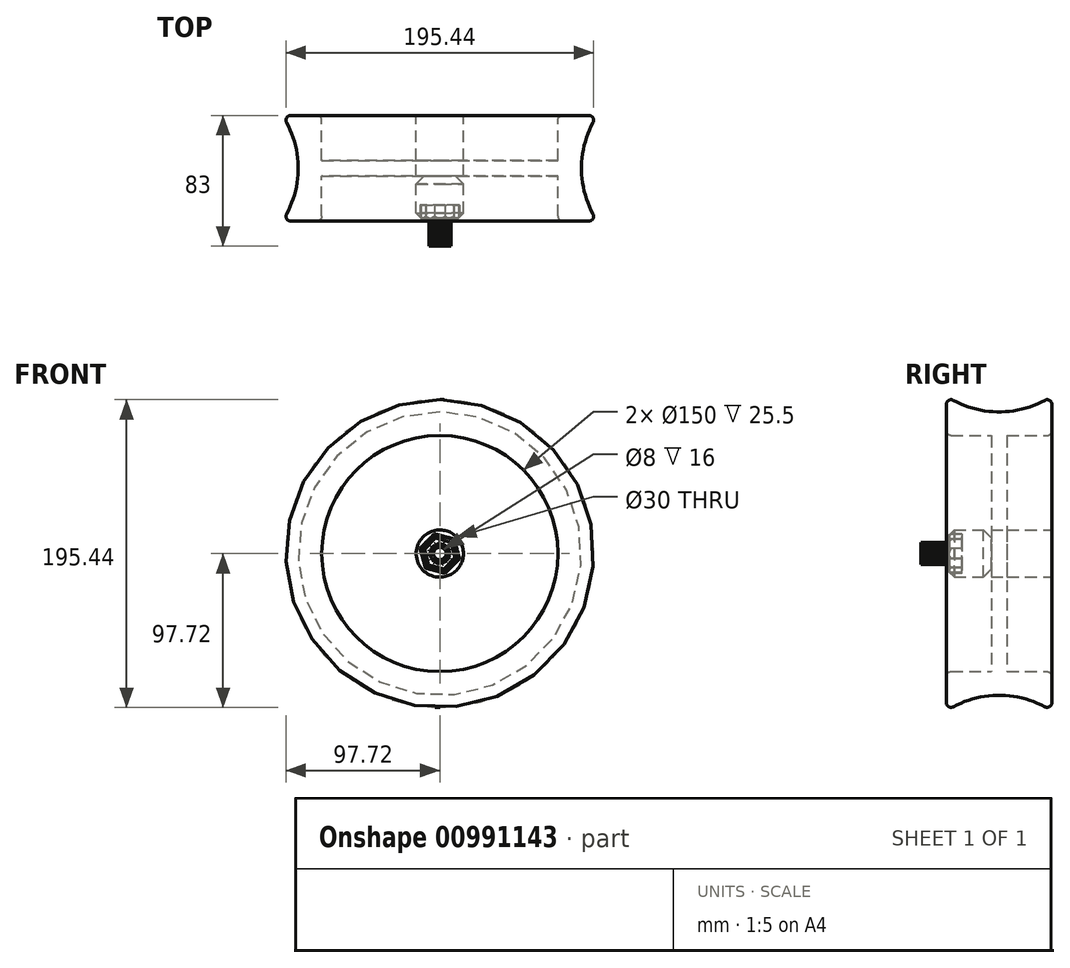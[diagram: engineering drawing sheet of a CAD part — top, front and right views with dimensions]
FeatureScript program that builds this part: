
annotation { "Feature Type Name" : "Feature", "Feature Type Description" : "" }
export const myFeature = defineFeature(function(context is Context, id is Id, definition is map)
    precondition{}
    {
        {
            var Q0;
            Q0=qCreatedBy(makeId("Right.planeOp"),FACE);
            var sketch = newSketch(context, id + "F0", { "sketchPlane" : qUnion([Q0])});
            skPoint(sketch, "E0", {"position": v(0, 90) * mm});
            skLineSegment(sketch, "E1.bottom", {"start": v(33.5, 100) * mm, "end": v(-33.5, 100) * mm});
            skLineSegment(sketch, "E1.top", {"start": v(33.5, 75) * mm, "end": v(-33.5, 75) * mm});
            skLineSegment(sketch, "E1.left", {"start": v(33.5, 100) * mm, "end": v(33.5, 75) * mm});
            skLineSegment(sketch, "E1.right", {"start": v(-33.5, 100) * mm, "end": v(-33.5, 75) * mm});
            skArc(sketch, "E2", {"start": v(-33.5, 100) * mm, "mid": v(0, 90) * mm, "end": v(33.5, 100) * mm});
            skLineSegment(sketch, "E3", {"start": v(33.5, 0) * mm, "end": v(-5, 0) * mm});
            skLineSegment(sketch, "E4", {"start": v(0, 0) * mm, "end": v(-5, 0) * mm});
            skLineSegment(sketch, "E5", {"start": v(-5, 0) * mm, "end": v(-5, 75) * mm});
            skLineSegment(sketch, "E6.MirrorCS", {"start": v(5, 0) * mm, "end": v(5, 75) * mm});
            skLineSegment(sketch, "E7", {"start": v(33.5, 0) * mm, "end": v(33.5, 15) * mm});
            skLineSegment(sketch, "E8", {"start": v(33.5, 15) * mm, "end": v(-5, 15) * mm});
            skSolve(sketch);
        }
        {
            var Q0;
            Q0=makeQuery(id+"F0.imprint","IMPRINT",FACE,{"disambiguationData":[TD([[makeQuery(id+"F0.imprint","IMPRINT",EDGE,{"derivedFrom":sQuery(id+"F0.wireOp",EDGE,"E1.top")}),-1.0]])]});
            var Q1;
            {var subQ1=sQuery(id+"F0.wireOp",EDGE,"E4");Q1=makeQuery(id+"F0.imprint","IMPRINT",FACE,{"disambiguationData":[TD([[makeQuery(id+"F0.imprint","IMPRINT",EDGE,{"derivedFrom":subQ1}),-1.0]])]});}
            var Q2;
            {var subQ0=sQuery(id+"F0.wireOp",EDGE,"jARXLERj-0qEw-X7Dj-GQ2f-9SWR6kces5kd");Q2=makeQuery(id+"F0.imprint","IMPRINT",FACE,{"disambiguationData":[TD([[makeQuery(id+"F0.imprint","IMPRINT",EDGE,{"derivedFrom":subQ0}),1.0]])]});}
            var Q3;
            {var subQ0=sQuery(id+"F0.wireOp",EDGE,"E7");Q3=makeQuery(id+"F0.imprint","IMPRINT",FACE,{"disambiguationData":[TD([[makeQuery(id+"F0.imprint","IMPRINT",EDGE,{"derivedFrom":subQ0}),1.0]])]});}
            var Q4;
            {var subQ0=sQuery(id+"F0.wireOp",EDGE,"E5");var subQ1=sQuery(id+"F0.wireOp",EDGE,"E1.top");var subQ2=makeQuery(id+"F0.imprint","INTERSECT",VERTEX,{"derivedFrom":[subQ1,subQ0]});Q4=makeQuery(id+"F0.imprint","IMPRINT",FACE,{"disambiguationData":[TD([[makeQuery(id+"F0.imprint","IMPRINT",EDGE,{"disambiguationData":[TD([[subQ2,1.0]])],"derivedFrom":subQ1}),1.0]])]});}
            var Q5;
            Q5=sQuery(id+"F0.wireOp",EDGE,"E3");
            revolve(context, id + "F1", {"surfaceOperationType" : NewSurfaceOperationType.NEW, "entities" : qUnion([Q0, Q1, Q2, Q3, Q4]), "axis" : qUnion([Q5]), "revolveType" : RevolveType.FULL});
        }
        {
            var Q0;
            Q0=makeQuery(id+"F1.opRevolve","SWEPT_EDGE",EDGE,{"disambiguationData":[OSD([sQuery(id+"F0.wireOp",EDGE,"E1.bottom"),sQuery(id+"F0.wireOp",EDGE,"E1.right"),sQuery(id+"F0.wireOp",EDGE,"E2")])]});
            var Q1;
            Q1=makeQuery(id+"F1.opRevolve","SWEPT_EDGE",EDGE,{"disambiguationData":[OSD([sQuery(id+"F0.wireOp",EDGE,"E1.bottom"),sQuery(id+"F0.wireOp",EDGE,"E1.left"),sQuery(id+"F0.wireOp",EDGE,"E2")])]});
            var Q2;
            Q2=makeQuery(id+"F1.opRevolve","SWEPT_EDGE",EDGE,{"disambiguationData":[OSD([sQuery(id+"F0.wireOp",EDGE,"E1.top"),sQuery(id+"F0.wireOp",EDGE,"E1.right")])]});
            var Q3;
            Q3=makeQuery(id+"F1.opRevolve","SWEPT_EDGE",EDGE,{"disambiguationData":[OSD([sQuery(id+"F0.wireOp",EDGE,"E1.top"),sQuery(id+"F0.wireOp",EDGE,"E1.left")])]});
            fillet(context, id + "F2", {"entities" : qUnion([Q0, Q1, Q2, Q3]), "radius" : 3 * mm, "tangentPropagation" : true, "allowEdgeOverflow" : false});
        }
        {
            var Q0;
            Q0=makeQuery(id+"F1.opRevolve","SWEPT_FACE",FACE,{"disambiguationData":[OSD([sQuery(id+"F0.wireOp",EDGE,"E5")])]});
            var sketch = newSketch(context, id + "F3", { "sketchPlane" : qUnion([Q0])});
            skCircle(sketch, "E9.0.0", {"center": v(0, 0) * mm, "radius": 15 * mm});
            skSolve(sketch);
        }
        {
            var Q0;
            Q0 = qSketchRegion(id + "F3", true);
            var Q1;
            Q1=makeQuery(id+"F1.opRevolve","SWEPT_FACE",FACE,{"disambiguationData":[OSD([sQuery(id+"F0.wireOp",EDGE,"E1.right")])]});
            extrude(context, id + "F4", {"entities" : qUnion([Q0]), "operationType" : NewBodyOperationType.ADD, "endBound" : BoundingType.UP_TO_SURFACE, "depth" : 25 * mm, "endBoundEntityFace" : qUnion([Q1]), "offsetDistance" : 25 * mm});
        }
        {
            var Q0;
            Q0=makeQuery(id+"F4.opExtrude","CAP_FACE",FACE,{"disambiguationData":[OSD([sQuery(id+"F3.wireOp",EDGE,"E9.0.0")])],"isStart":false});
            var sketch = newSketch(context, id + "F5", { "sketchPlane" : qUnion([Q0])});
            skCircle(sketch, "E10.0", {"center": v(0, 0) * mm, "radius": 15 * mm});
            skCircle(sketch, "E11.cCircle", {"center": v(0, 0) * mm, "radius": 12.42 * mm, "construction": true});
            skLineSegment(sketch, "E11.0", {"start": v(8.74, 8.83) * mm, "end": v(12.02, -3.15) * mm});
            skLineSegment(sketch, "E11.1", {"start": v(12.02, -3.15) * mm, "end": v(3.28, -11.98) * mm});
            skLineSegment(sketch, "E11.2", {"start": v(3.28, -11.98) * mm, "end": v(-8.74, -8.83) * mm});
            skLineSegment(sketch, "E11.3", {"start": v(-8.74, -8.83) * mm, "end": v(-12.02, 3.15) * mm});
            skLineSegment(sketch, "E11.4", {"start": v(-12.02, 3.15) * mm, "end": v(-3.28, 11.98) * mm});
            skLineSegment(sketch, "E11.5", {"start": v(-3.28, 11.98) * mm, "end": v(8.74, 8.83) * mm});
            skLineSegment(sketch, "E12.0", {"start": v(3.43, -12.54) * mm, "end": v(-9.15, -9.24) * mm});
            skLineSegment(sketch, "E12.1", {"start": v(-12.57, 3.3) * mm, "end": v(-3.43, 12.54) * mm});
            skLineSegment(sketch, "E12.2", {"start": v(-3.43, 12.54) * mm, "end": v(9.15, 9.24) * mm});
            skLineSegment(sketch, "E12.3", {"start": v(-9.15, -9.24) * mm, "end": v(-12.57, 3.3) * mm});
            skLineSegment(sketch, "E12.4", {"start": v(9.15, 9.24) * mm, "end": v(12.57, -3.3) * mm});
            skLineSegment(sketch, "E12.5", {"start": v(12.57, -3.3) * mm, "end": v(3.43, -12.54) * mm});
            skSolve(sketch);
        }
        {
            var Q0;
            Q0=sQuery(id+"F5.wireOp",VERTEX,"E10.0.center");
            var Q1;
            Q1=makeQuery(id+"F1.opRevolve","SWEPT_BODY",BODY,{"disambiguationData":[OSD([sQuery(id+"F0.wireOp",EDGE,"E1.top"),sQuery(id+"F0.wireOp",EDGE,"E1.left"),sQuery(id+"F0.wireOp",EDGE,"E1.right"),sQuery(id+"F0.wireOp",EDGE,"E2"),sQuery(id+"F0.wireOp",EDGE,"E3"),sQuery(id+"F0.wireOp",EDGE,"E4"),sQuery(id+"F0.wireOp",EDGE,"E5"),sQuery(id+"F0.wireOp",EDGE,"E6.MirrorCS"),sQuery(id+"F0.wireOp",EDGE,"E7"),sQuery(id+"F0.wireOp",EDGE,"E8"),sQuery(id+"F0.wireOp",EDGE,"jARXLERj-0qEw-X7Dj-GQ2f-9SWR6kces5kd")])]});
            hole(context, id + "F6", {"style" : HoleStyle.SIMPLE, "endStyle" : HoleEndStyle.THROUGH, "holeDiameter" : 8 * mm, "majorDiameter" : 5 * mm, "isTappedThrough" : true, "tappedDepth" : 12 * mm, "tapClearance" : 3, "locations" : qUnion([Q0]), "scope" : qUnion([Q1])});
        }
        {
            var Q0;
            Q0=makeQuery(id+"F5.imprint","IMPRINT",FACE,{"disambiguationData":[TD([[makeQuery(id+"F5.imprint","IMPRINT",EDGE,{"derivedFrom":sQuery(id+"F5.wireOp",EDGE,"E11.0")}),1.0]])]});
            var Q1;
            Q1=makeQuery(id+"F5.imprint","IMPRINT",FACE,{"disambiguationData":[TD([[makeQuery(id+"F5.imprint","IMPRINT",EDGE,{"derivedFrom":sQuery(id+"F5.wireOp",EDGE,"E11.0")}),-1.0]])]});
            extrude(context, id + "F7", {"entities" : qUnion([Q0, Q1]), "operationType" : NewBodyOperationType.REMOVE, "oppositeDirection" : true, "depth" : 10 * mm, "offsetDistance" : 10 * mm});
        }
        {
            var Q0;
            Q0=makeQuery(id+"F4.opExtrude","CAP_EDGE",EDGE,{"disambiguationData":[OSD([sQuery(id+"F3.wireOp",EDGE,"E9.0.0")])],"isStart":true});
            chamfer(context, id + "F8", {"entities" : qUnion([Q0]), "width" : 5 * mm, "tangentPropagation" : true});
        }
        {
            var Q0;
            Q0=makeQuery(id+"F4.opExtrude","CAP_EDGE",EDGE,{"disambiguationData":[OSD([sQuery(id+"F3.wireOp",EDGE,"E9.0.0")])],"isStart":false});
            chamfer(context, id + "F9", {"entities" : qUnion([Q0]), "width" : 5 * mm, "tangentPropagation" : true});
        }
        {
            var Q0;
            Q0=makeQuery(id+"F5.imprint","IMPRINT",FACE,{"disambiguationData":[TD([[makeQuery(id+"F5.imprint","IMPRINT",EDGE,{"derivedFrom":sQuery(id+"F5.wireOp",EDGE,"E11.0")}),-1.0]])]});
            extrude(context, id + "F10", {"entities" : qUnion([Q0]), "oppositeDirection" : true, "depth" : 10 * mm, "offsetDistance" : 25 * mm});
        }
        {
            var Q0;
            Q0=makeQuery(id+"F10.opExtrude","CAP_EDGE",EDGE,{"disambiguationData":[OSD([sQuery(id+"F5.wireOp",EDGE,"E11.5")])],"isStart":true});
            var Q1;
            Q1=makeQuery(id+"F10.opExtrude","CAP_EDGE",EDGE,{"disambiguationData":[OSD([sQuery(id+"F5.wireOp",EDGE,"E11.4")])],"isStart":true});
            var Q2;
            Q2=makeQuery(id+"F10.opExtrude","CAP_EDGE",EDGE,{"disambiguationData":[OSD([sQuery(id+"F5.wireOp",EDGE,"E11.3")])],"isStart":true});
            var Q3;
            Q3=makeQuery(id+"F10.opExtrude","CAP_EDGE",EDGE,{"disambiguationData":[OSD([sQuery(id+"F5.wireOp",EDGE,"E11.2")])],"isStart":true});
            var Q4;
            Q4=makeQuery(id+"F10.opExtrude","CAP_EDGE",EDGE,{"disambiguationData":[OSD([sQuery(id+"F5.wireOp",EDGE,"E11.1")])],"isStart":true});
            var Q5;
            Q5=makeQuery(id+"F10.opExtrude","CAP_EDGE",EDGE,{"disambiguationData":[OSD([sQuery(id+"F5.wireOp",EDGE,"E11.0")])],"isStart":true});
            chamfer(context, id + "F11", {"entities" : qUnion([Q0, Q1, Q2, Q3, Q4, Q5]), "width" : 2 * mm, "tangentPropagation" : true});
        }
        {
            var Q0;
            Q0=makeQuery(id+"F5.imprint","IMPRINT",FACE,{"disambiguationData":[TD([[makeQuery(id+"F5.imprint","IMPRINT",EDGE,{"derivedFrom":sQuery(id+"F5.wireOp",EDGE,"E11.0")}),-1.0]])]});
            var sketch = newSketch(context, id + "F12", { "sketchPlane" : qUnion([Q0])});
            skPoint(sketch, "E13.0", {"position": v(0, 0) * mm});
            skCircle(sketch, "E14", {"center": v(0, 0) * mm, "radius": 6.97 * mm, "construction": true});
            skLineSegment(sketch, "E15", {"start": v(0, 0) * mm, "end": v(0, 6.97) * mm, "construction": true});
            skLineSegment(sketch, "E16", {"start": v(0, 0) * mm, "end": v(-2.84, 6.37) * mm, "construction": true});
            skLineSegment(sketch, "E17", {"start": v(0, 6.97) * mm, "end": v(-0.7, 6.94) * mm});
            skLineSegment(sketch, "E18", {"start": v(-0.7, 6.94) * mm, "end": v(-2.84, 6.37) * mm, "construction": true});
            skPoint(sketch, "E19", {"position": v(-1.77, 6.66) * mm});
            skLineSegment(sketch, "E20", {"start": v(-1.79, 4.79) * mm, "end": v(-0.82, 5.04) * mm});
            skPoint(sketch, "E21", {"position": v(-1.3, 4.92) * mm});
            skLineSegment(sketch, "E22", {"start": v(-1.77, 6.66) * mm, "end": v(-1.3, 4.92) * mm, "construction": true});
            skLineSegment(sketch, "E23", {"start": v(-0.7, 6.94) * mm, "end": v(-0.82, 5.04) * mm});
            skLineSegment(sketch, "E24", {"start": v(-1.79, 4.79) * mm, "end": v(-2.84, 6.37) * mm});
            skLineSegment(sketch, "E25.1.0", {"start": v(-3.58, 3.65) * mm, "end": v(-2.8, 4.27) * mm});
            skLineSegment(sketch, "E25.1.1", {"start": v(-3.58, 3.65) * mm, "end": v(-5.18, 4.67) * mm});
            skLineSegment(sketch, "E25.1.2", {"start": v(-3.46, 6.05) * mm, "end": v(-2.8, 4.27) * mm});
            skLineSegment(sketch, "E25.1.3", {"start": v(-2.84, 6.37) * mm, "end": v(-3.46, 6.05) * mm});
            skLineSegment(sketch, "E25.2.0", {"start": v(-4.75, 1.87) * mm, "end": v(-4.3, 2.76) * mm});
            skLineSegment(sketch, "E25.2.1", {"start": v(-4.75, 1.87) * mm, "end": v(-6.63, 2.16) * mm});
            skLineSegment(sketch, "E25.2.2", {"start": v(-5.62, 4.12) * mm, "end": v(-4.3, 2.76) * mm});
            skLineSegment(sketch, "E25.2.3", {"start": v(-5.18, 4.67) * mm, "end": v(-5.62, 4.12) * mm});
            skLineSegment(sketch, "E25.3.0", {"start": v(-5.1, -0.22) * mm, "end": v(-5.05, 0.78) * mm});
            skLineSegment(sketch, "E25.3.1", {"start": v(-5.1, -0.22) * mm, "end": v(-6.94, -0.73) * mm});
            skLineSegment(sketch, "E25.3.2", {"start": v(-6.82, 1.48) * mm, "end": v(-5.05, 0.78) * mm});
            skLineSegment(sketch, "E25.3.3", {"start": v(-6.63, 2.16) * mm, "end": v(-6.82, 1.48) * mm});
            skLineSegment(sketch, "E25.4.0", {"start": v(-4.57, -2.28) * mm, "end": v(-4.93, -1.35) * mm});
            skLineSegment(sketch, "E25.4.1", {"start": v(-4.57, -2.28) * mm, "end": v(-6.04, -3.49) * mm});
            skLineSegment(sketch, "E25.4.2", {"start": v(-6.83, -1.42) * mm, "end": v(-4.93, -1.35) * mm});
            skLineSegment(sketch, "E25.4.3", {"start": v(-6.94, -0.73) * mm, "end": v(-6.83, -1.42) * mm});
            skLineSegment(sketch, "E25.5.0", {"start": v(-3.25, -3.94) * mm, "end": v(-3.96, -3.23) * mm});
            skLineSegment(sketch, "E25.5.1", {"start": v(-3.25, -3.94) * mm, "end": v(-4.1, -5.64) * mm});
            skLineSegment(sketch, "E25.5.2", {"start": v(-5.66, -4.07) * mm, "end": v(-3.96, -3.23) * mm});
            skLineSegment(sketch, "E25.5.3", {"start": v(-6.04, -3.49) * mm, "end": v(-5.66, -4.07) * mm});
            skLineSegment(sketch, "E25.6.0", {"start": v(-1.37, -4.92) * mm, "end": v(-2.3, -4.56) * mm});
            skLineSegment(sketch, "E25.6.1", {"start": v(-1.37, -4.92) * mm, "end": v(-1.45, -6.82) * mm});
            skLineSegment(sketch, "E25.6.2", {"start": v(-3.51, -6.02) * mm, "end": v(-2.3, -4.56) * mm});
            skLineSegment(sketch, "E25.6.3", {"start": v(-4.1, -5.64) * mm, "end": v(-3.51, -6.02) * mm});
            skLineSegment(sketch, "E25.7.0", {"start": v(0.75, -5.05) * mm, "end": v(-0.24, -5.1) * mm});
            skLineSegment(sketch, "E25.7.1", {"start": v(0.75, -5.05) * mm, "end": v(1.45, -6.82) * mm});
            skLineSegment(sketch, "E25.7.2", {"start": v(-0.76, -6.93) * mm, "end": v(-0.24, -5.1) * mm});
            skLineSegment(sketch, "E25.7.3", {"start": v(-1.45, -6.82) * mm, "end": v(-0.76, -6.93) * mm});
            skLineSegment(sketch, "E25.8.0", {"start": v(2.75, -4.31) * mm, "end": v(1.85, -4.76) * mm});
            skLineSegment(sketch, "E25.8.1", {"start": v(2.75, -4.31) * mm, "end": v(4.1, -5.64) * mm});
            skLineSegment(sketch, "E25.8.2", {"start": v(2.13, -6.64) * mm, "end": v(1.85, -4.76) * mm});
            skLineSegment(sketch, "E25.8.3", {"start": v(1.45, -6.82) * mm, "end": v(2.13, -6.64) * mm});
            skLineSegment(sketch, "E25.9.0", {"start": v(4.26, -2.82) * mm, "end": v(3.63, -3.6) * mm});
            skLineSegment(sketch, "E25.9.1", {"start": v(4.26, -2.82) * mm, "end": v(6.04, -3.49) * mm});
            skLineSegment(sketch, "E25.9.2", {"start": v(4.64, -5.2) * mm, "end": v(3.63, -3.6) * mm});
            skLineSegment(sketch, "E25.9.3", {"start": v(4.1, -5.64) * mm, "end": v(4.64, -5.2) * mm});
            skLineSegment(sketch, "E25.10.0", {"start": v(5.04, -0.84) * mm, "end": v(4.78, -1.8) * mm});
            skLineSegment(sketch, "E25.10.1", {"start": v(5.04, -0.84) * mm, "end": v(6.94, -0.73) * mm});
            skLineSegment(sketch, "E25.10.2", {"start": v(6.36, -2.86) * mm, "end": v(4.78, -1.8) * mm});
            skLineSegment(sketch, "E25.10.3", {"start": v(6.04, -3.49) * mm, "end": v(6.36, -2.86) * mm});
            skLineSegment(sketch, "E25.11.0", {"start": v(4.95, 1.28) * mm, "end": v(5.1, 0.3) * mm});
            skLineSegment(sketch, "E25.11.1", {"start": v(4.95, 1.28) * mm, "end": v(6.63, 2.16) * mm});
            skLineSegment(sketch, "E25.11.2", {"start": v(6.97, -0.03) * mm, "end": v(5.1, 0.3) * mm});
            skLineSegment(sketch, "E25.11.3", {"start": v(6.94, -0.73) * mm, "end": v(6.97, -0.03) * mm});
            skLineSegment(sketch, "E25.12.0", {"start": v(4, 3.18) * mm, "end": v(4.54, 2.34) * mm});
            skLineSegment(sketch, "E25.12.1", {"start": v(4, 3.18) * mm, "end": v(5.18, 4.67) * mm});
            skLineSegment(sketch, "E25.12.2", {"start": v(6.38, 2.8) * mm, "end": v(4.54, 2.34) * mm});
            skLineSegment(sketch, "E25.12.3", {"start": v(6.63, 2.16) * mm, "end": v(6.38, 2.8) * mm});
            skLineSegment(sketch, "E25.13.0", {"start": v(2.36, 4.53) * mm, "end": v(3.2, 3.99) * mm});
            skLineSegment(sketch, "E25.13.1", {"start": v(2.36, 4.53) * mm, "end": v(2.84, 6.37) * mm});
            skLineSegment(sketch, "E25.13.2", {"start": v(4.69, 5.16) * mm, "end": v(3.2, 3.99) * mm});
            skLineSegment(sketch, "E25.13.3", {"start": v(5.18, 4.67) * mm, "end": v(4.69, 5.16) * mm});
            skLineSegment(sketch, "E25.14.0", {"start": v(0.31, 5.1) * mm, "end": v(1.3, 4.94) * mm});
            skLineSegment(sketch, "E25.14.1", {"start": v(0.31, 5.1) * mm, "end": v(0, 6.97) * mm});
            skLineSegment(sketch, "E25.14.2", {"start": v(2.18, 6.62) * mm, "end": v(1.3, 4.94) * mm});
            skLineSegment(sketch, "E25.14.3", {"start": v(2.84, 6.37) * mm, "end": v(2.18, 6.62) * mm});
            skCircle(sketch, "E26.0", {"center": v(0, 0) * mm, "radius": 4 * mm});
            skSolve(sketch);
        }
        {
            var Q0;
            Q0=makeQuery(id+"F12.imprint","IMPRINT",FACE,{"disambiguationData":[TD([[makeQuery(id+"F12.imprint","IMPRINT",EDGE,{"derivedFrom":sQuery(id+"F12.wireOp",EDGE,"E17")}),1.0]])]});
            extrude(context, id + "F13", {"entities" : qUnion([Q0]), "operationType" : NewBodyOperationType.ADD, "oppositeDirection" : true, "depth" : 10 * mm, "offsetDistance" : 25 * mm});
        }
        {
            var Q0;
            Q0=makeQuery(id+"F12.imprint","IMPRINT",FACE,{"disambiguationData":[TD([[makeQuery(id+"F12.imprint","IMPRINT",EDGE,{"derivedFrom":sQuery(id+"F12.wireOp",EDGE,"E17")}),1.0]])]});
            extrude(context, id + "F14", {"entities" : qUnion([Q0]), "operationType" : NewBodyOperationType.ADD, "depth" : 16 * mm, "offsetDistance" : 25 * mm});
        }
    });
